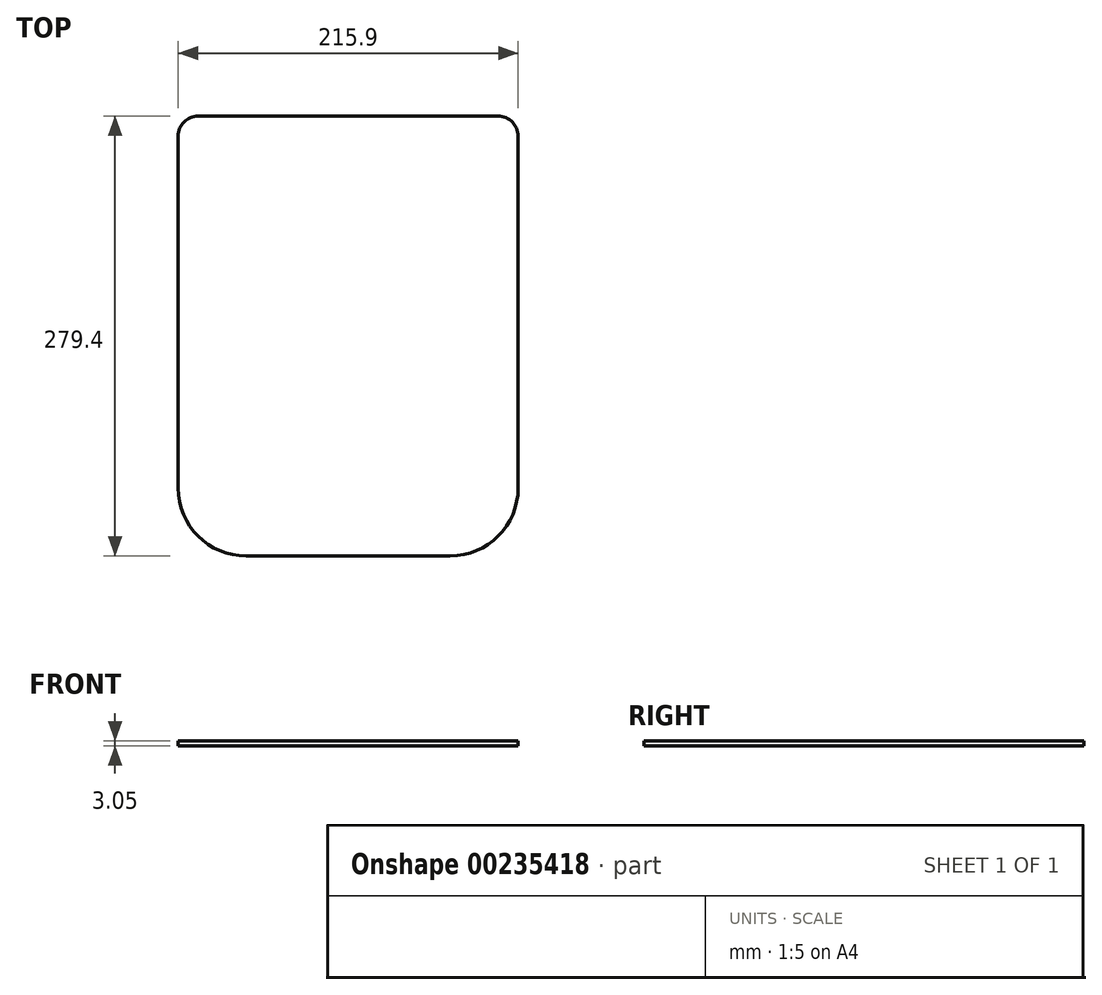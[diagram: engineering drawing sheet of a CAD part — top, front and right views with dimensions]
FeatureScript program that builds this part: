
annotation { "Feature Type Name" : "Feature", "Feature Type Description" : "" }
export const myFeature = defineFeature(function(context is Context, id is Id, definition is map)
    precondition{}
    {
        {
            var Q0;
            Q0=qCreatedBy(makeId("Top.planeOp"),FACE);
            var sketch = newSketch(context, id + "F0", { "sketchPlane" : qUnion([Q0])});
            skLineSegment(sketch, "E0.bottom", {"start": v(-107.95, 139.7) * mm, "end": v(107.95, 139.7) * mm});
            skLineSegment(sketch, "E0.top", {"start": v(-107.95, -139.7) * mm, "end": v(107.95, -139.7) * mm});
            skLineSegment(sketch, "E0.left", {"start": v(-107.95, 139.7) * mm, "end": v(-107.95, -139.7) * mm});
            skLineSegment(sketch, "E0.right", {"start": v(107.95, 139.7) * mm, "end": v(107.95, -139.7) * mm});
            skPoint(sketch, "E0.middle", {"position": v(0, 0) * mm});
            skSolve(sketch);
        }
        {
            var Q0;
            Q0 = qSketchRegion(id + "F0", true);
            extrude(context, id + "F1", {"entities" : qUnion([Q0]), "depth" : 3.05 * mm});
        }
        {
            var Q0;
            Q0=makeQuery(id+"F1.opExtrude","SWEPT_EDGE",EDGE,{"disambiguationData":[OSD([sQuery(id+"F0.wireOp",EDGE,"E0.top"),sQuery(id+"F0.wireOp",EDGE,"E0.left")])]});
            var Q1;
            Q1=makeQuery(id+"F1.opExtrude","SWEPT_EDGE",EDGE,{"disambiguationData":[OSD([sQuery(id+"F0.wireOp",EDGE,"E0.top"),sQuery(id+"F0.wireOp",EDGE,"E0.right")])]});
            fillet(context, id + "F2", {"entities" : qUnion([Q0, Q1]), "radius" : 43.18 * mm, "tangentPropagation" : true, "allowEdgeOverflow" : false});
        }
        {
            var Q0;
            Q0=makeQuery(id+"F1.opExtrude","SWEPT_EDGE",EDGE,{"disambiguationData":[OSD([sQuery(id+"F0.wireOp",EDGE,"E0.bottom"),sQuery(id+"F0.wireOp",EDGE,"E0.left")])]});
            var Q1;
            Q1=makeQuery(id+"F1.opExtrude","SWEPT_EDGE",EDGE,{"disambiguationData":[OSD([sQuery(id+"F0.wireOp",EDGE,"E0.bottom"),sQuery(id+"F0.wireOp",EDGE,"E0.right")])]});
            fillet(context, id + "F3", {"entities" : qUnion([Q0, Q1]), "radius" : 12.7 * mm, "tangentPropagation" : true, "allowEdgeOverflow" : false});
        }
    });
